# Revit family: РИДАН_Реле давления(KPI35R_KPI36R_KPI38R)
name_source: partatom
category: Арматура трубопроводов
units: mm (PartAtom-declared; Revit-internal decimal feet)

## family parameters
Всегда вертикально = Да
На основе рабочей плоскости = Нет
Общий = Нет
При загрузке вырезать с полостями = Нет
Размер круглого соединителя = Использовать диаметр
Тип детали = Нормальный

## types (5) — shared parameters
ADSK_Версия Revit = 2019
ADSK_Версия семейства = 1.0
ADSK_Единица измерения = шт.
ADSK_Завод-изготовитель = ООО «Ридан-Трейд»
ADSK_Количество = 1
ADSK_Масса = 0.3

## per-type parameters (varying)
| type | ADSK_Код изделия | ADSK_Марка | ADSK_Наименование | a | b |
| КРI35R 060-121766R | 060-121766R | КРI35R | Реле давления KPI 35R, диапазон настройки -0,2...7,5 бар, дифференциал 0,7…4 бар, штуцер G1/4А, автоматический сброс | 7 мм | 12 мм |
| КРI35R 060-132466R | 060-132466R | КРI35R | Реле давления KPI 35R, диапазон настройки -0,2...7,5 бар, дифференциал 0,7…4 бар, штуцер G1/2А, автоматический сброс | 10 мм | 15 мм |
| КРI35R 060-132566R | 060-132566R | КРI35R | Реле давления KPI 35R, диапазон настройки -0,2...8 бар, дифференциал 0,4…1,5 бар, штуцер G1/2А, автоматический сброс | 10 мм | 15 мм |
| KPI36R 060-118966R | 060-118966R | KPI36R | Реле давления KPI 36R, диапазон настройки 2...14 бар, дифференциал 1…4 бар, штуцер G1/4А, автоматический сброс | 7 мм | 12 мм |
| KPI38R 060-508166R | 060-508166R | KPI38R | Реле давления KPI 38R, диапазон настройки 8...32 бар, дифференциал 2…6 бар, штуцер G1/4А, автоматический сброс | 7 мм | 12 мм |
